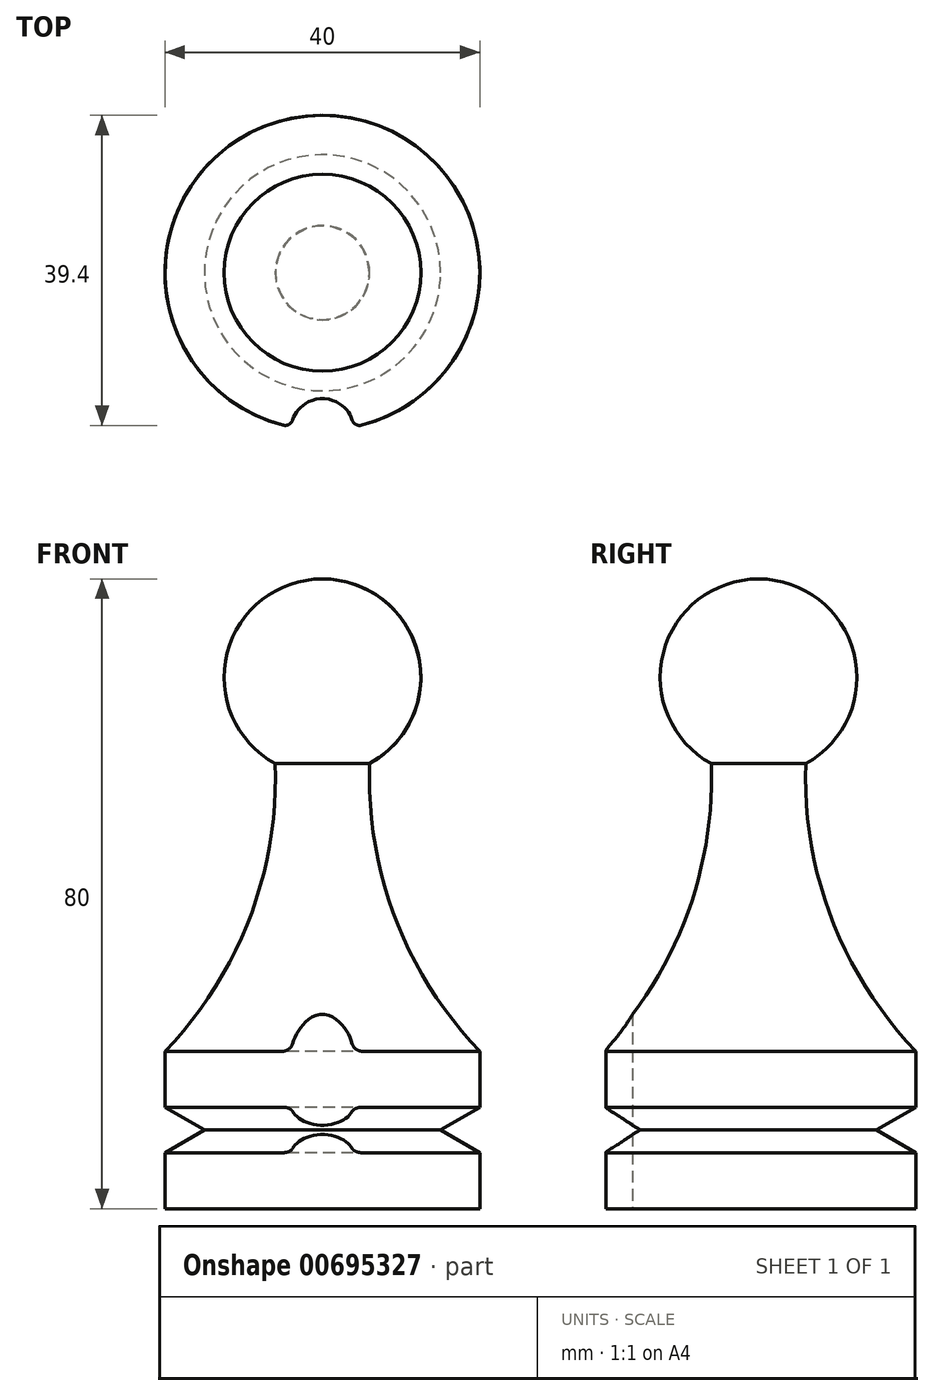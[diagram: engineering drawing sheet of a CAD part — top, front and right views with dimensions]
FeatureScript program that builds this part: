
annotation { "Feature Type Name" : "Feature", "Feature Type Description" : "" }
export const myFeature = defineFeature(function(context is Context, id is Id, definition is map)
    precondition{}
    {
        {
            var Q0;
            Q0=qCreatedBy(makeId("Front.planeOp"),FACE);
            var sketch = newSketch(context, id + "F0", { "sketchPlane" : qUnion([Q0])});
            skLineSegment(sketch, "E0", {"start": v(0, 84.5) * mm, "end": v(0, -76.94) * mm, "construction": true});
            skLineSegment(sketch, "E1", {"start": v(0, 0) * mm, "end": v(20, 0) * mm});
            skLineSegment(sketch, "E2", {"start": v(20, 0) * mm, "end": v(20, 12.89) * mm});
            skLineSegment(sketch, "E3", {"start": v(20, 12.89) * mm, "end": v(15, 10) * mm});
            skLineSegment(sketch, "E4", {"start": v(15, 10) * mm, "end": v(20, 7.11) * mm});
            skLineSegment(sketch, "E5", {"start": v(20, 7.11) * mm, "end": v(20, 20) * mm});
            skArc(sketch, "E6", {"start": v(6, 56.53) * mm, "mid": v(9.28, 36.84) * mm, "end": v(20, 20) * mm});
            skArc(sketch, "E7", {"start": v(6, 56.53) * mm, "mid": v(12.11, 70.6) * mm, "end": v(0, 80) * mm});
            skLineSegment(sketch, "E8", {"start": v(0, 80) * mm, "end": v(0, 0) * mm});
            skSolve(sketch);
        }
        {
            var Q0;
            Q0=makeQuery(id+"F0.imprint","IMPRINT",FACE,{"disambiguationData":[TD([[makeQuery(id+"F0.imprint","IMPRINT",EDGE,{"derivedFrom":sQuery(id+"F0.wireOp",EDGE,"E1")}),1.0]])]});
            var Q1;
            Q1=sQuery(id+"F0.wireOp",EDGE,"E0");
            revolve(context, id + "F1", {"entities" : qUnion([Q0]), "axis" : qUnion([Q1]), "revolveType" : RevolveType.FULL});
        }
        {
            var Q0;
            Q0=makeQuery(id+"F1.opRevolve","SWEPT_FACE",FACE,{"disambiguationData":[OSD([sQuery(id+"F0.wireOp",EDGE,"E1")])]});
            var sketch = newSketch(context, id + "F2", { "sketchPlane" : qUnion([Q0])});
            skCircle(sketch, "E9", {"center": v(0, 20) * mm, "radius": 4 * mm});
            skSolve(sketch);
        }
        {
            var Q0;
            {var subQ0=sQuery(id+"F2.wireOp",EDGE,"E9");var subQ1=makeQuery(id+"F1.opRevolve","SWEPT_EDGE",EDGE,{"disambiguationData":[OSD([sQuery(id+"F0.wireOp",EDGE,"E1"),sQuery(id+"F0.wireOp",EDGE,"E2")])]});var subQ2=makeQuery(id+"F2.imprint","INTERSECT",VERTEX,{"disambiguationData":[OD(0.0)],"derivedFrom":[subQ1,subQ0]});Q0=makeQuery(id+"F2.imprint","IMPRINT",FACE,{"disambiguationData":[TD([[makeQuery(id+"F2.imprint","IMPRINT",EDGE,{"disambiguationData":[TD([[subQ2,1.0]])],"derivedFrom":subQ0}),1.0]])]});}
            var Q1;
            {var subQ0=sQuery(id+"F2.wireOp",EDGE,"E9");var subQ1=makeQuery(id+"F1.opRevolve","SWEPT_EDGE",EDGE,{"disambiguationData":[OSD([sQuery(id+"F0.wireOp",EDGE,"E1"),sQuery(id+"F0.wireOp",EDGE,"E2")])]});var subQ2=makeQuery(id+"F2.imprint","INTERSECT",VERTEX,{"disambiguationData":[OD(0.0)],"derivedFrom":[subQ1,subQ0]});Q1=makeQuery(id+"F2.imprint","IMPRINT",FACE,{"disambiguationData":[TD([[makeQuery(id+"F2.imprint","IMPRINT",EDGE,{"disambiguationData":[TD([[subQ2,-1.0]])],"derivedFrom":subQ0}),1.0]])]});}
            extrude(context, id + "F3", {"entities" : qUnion([Q0, Q1]), "operationType" : NewBodyOperationType.REMOVE, "oppositeDirection" : true, "depth" : 25 * mm, "offsetDistance" : 25 * mm});
        }
        {
            var Q0;
            Q0=makeQuery(id+"F3.boolean.opBoolean","INTERSECT",EDGE,{"disambiguationData":[OD(0.0)],"derivedFrom":[makeQuery(id+"F1.opRevolve","SWEPT_FACE",FACE,{"disambiguationData":[OSD([sQuery(id+"F0.wireOp",EDGE,"E5")])]}),makeQuery(id+"F3.opExtrude","SWEPT_FACE",FACE,{"disambiguationData":[OSD([sQuery(id+"F2.wireOp",EDGE,"E9")])]})]});
            var Q1;
            Q1=makeQuery(id+"F3.boolean.opBoolean","INTERSECT",EDGE,{"disambiguationData":[OD(1.0)],"derivedFrom":[makeQuery(id+"F1.opRevolve","SWEPT_FACE",FACE,{"disambiguationData":[OSD([sQuery(id+"F0.wireOp",EDGE,"E5")])]}),makeQuery(id+"F3.opExtrude","SWEPT_FACE",FACE,{"disambiguationData":[OSD([sQuery(id+"F2.wireOp",EDGE,"E9")])]})]});
            var Q2;
            Q2=makeQuery(id+"F3.boolean.opBoolean","INTERSECT",EDGE,{"disambiguationData":[OD(1.0)],"derivedFrom":[makeQuery(id+"F1.opRevolve","SWEPT_FACE",FACE,{"disambiguationData":[OSD([sQuery(id+"F0.wireOp",EDGE,"E2")])]}),makeQuery(id+"F3.opExtrude","SWEPT_FACE",FACE,{"disambiguationData":[OSD([sQuery(id+"F2.wireOp",EDGE,"E9")])]})]});
            var Q3;
            Q3=makeQuery(id+"F3.boolean.opBoolean","INTERSECT",EDGE,{"disambiguationData":[OD(0.0)],"derivedFrom":[makeQuery(id+"F1.opRevolve","SWEPT_FACE",FACE,{"disambiguationData":[OSD([sQuery(id+"F0.wireOp",EDGE,"E2")])]}),makeQuery(id+"F3.opExtrude","SWEPT_FACE",FACE,{"disambiguationData":[OSD([sQuery(id+"F2.wireOp",EDGE,"E9")])]})]});
            fillet(context, id + "F4", {"entities" : qUnion([Q0, Q1, Q2, Q3]), "radius" : 1 * mm, "tangentPropagation" : true, "allowEdgeOverflow" : false});
        }
    });
